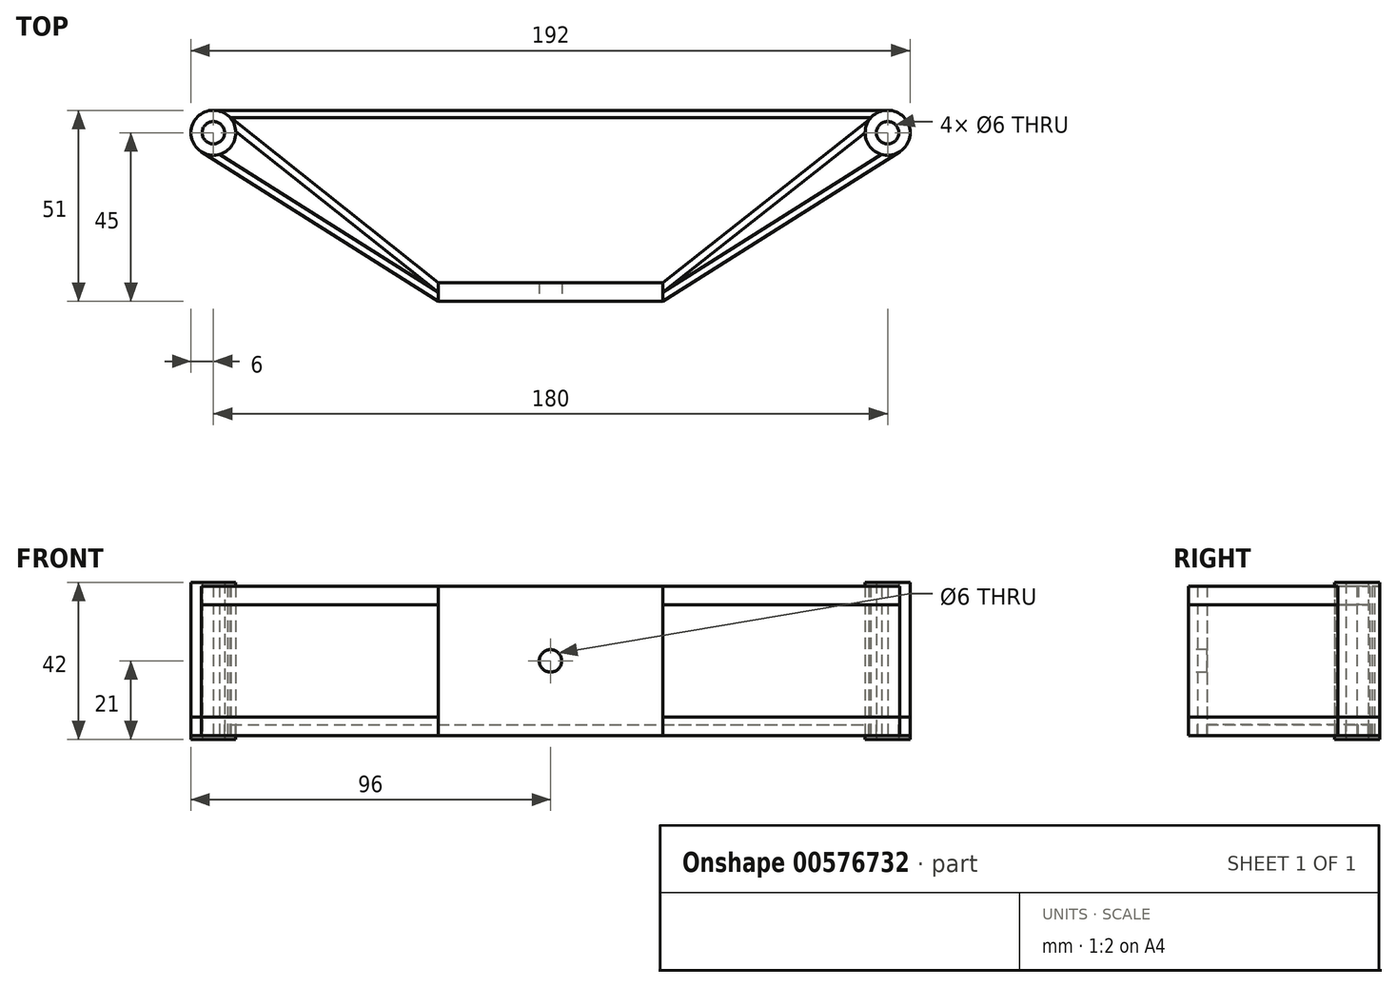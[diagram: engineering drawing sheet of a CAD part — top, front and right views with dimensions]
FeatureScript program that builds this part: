
annotation { "Feature Type Name" : "Feature", "Feature Type Description" : "" }
export const myFeature = defineFeature(function(context is Context, id is Id, definition is map)
    precondition{}
    {
        {
            var Q0;
            Q0=qCreatedBy(makeId("Top.planeOp"),FACE);
            var sketch = newSketch(context, id + "F0", { "sketchPlane" : qUnion([Q0])});
            skLineSegment(sketch, "E0.bottom", {"start": v(-30, 0) * mm, "end": v(30, 0) * mm});
            skLineSegment(sketch, "E0.top", {"start": v(-30, 5) * mm, "end": v(30, 5) * mm});
            skLineSegment(sketch, "E0.left", {"start": v(-30, 0) * mm, "end": v(-30, 5) * mm});
            skLineSegment(sketch, "E0.right", {"start": v(30, 0) * mm, "end": v(30, 5) * mm});
            skCircle(sketch, "E1", {"center": v(-90, 45) * mm, "radius": 3 * mm});
            skCircle(sketch, "E2", {"center": v(-90, 45) * mm, "radius": 6 * mm});
            skCircle(sketch, "E3", {"center": v(90, 45) * mm, "radius": 3 * mm});
            skCircle(sketch, "E4", {"center": v(90, 45) * mm, "radius": 6 * mm});
            skLineSegment(sketch, "E5", {"start": v(30, 0) * mm, "end": v(93.2, 39.93) * mm});
            skLineSegment(sketch, "E6", {"start": v(30, 5) * mm, "end": v(85.02, 48.35) * mm});
            skLineSegment(sketch, "E7", {"start": v(-30, 0) * mm, "end": v(-93.2, 39.93) * mm});
            skLineSegment(sketch, "E8", {"start": v(-90, 51) * mm, "end": v(90, 51) * mm});
            skLineSegment(sketch, "E9", {"start": v(-86.27, 49.7) * mm, "end": v(-30, 5) * mm});
            skLineSegment(sketch, "E10", {"start": v(-88.36, 39.23) * mm, "end": v(-30, 2.37) * mm});
            skLineSegment(sketch, "E11", {"start": v(-84.01, 45.35) * mm, "end": v(-30, 2.45) * mm});
            skLineSegment(sketch, "E12", {"start": v(84, 45) * mm, "end": v(30, 2.45) * mm});
            skLineSegment(sketch, "E13", {"start": v(88.36, 39.23) * mm, "end": v(30, 2.37) * mm});
            skLineSegment(sketch, "E14", {"start": v(-85.53, 49) * mm, "end": v(85.53, 49) * mm});
            skSolve(sketch);
        }
        {
            var Q0;
            Q0=makeQuery(id+"F0.imprint","IMPRINT",FACE,{"disambiguationData":[TD([[makeQuery(id+"F0.imprint","IMPRINT",EDGE,{"derivedFrom":sQuery(id+"F0.wireOp",EDGE,"E1")}),-1.0]])]});
            var Q1;
            Q1=makeQuery(id+"F0.imprint","IMPRINT",FACE,{"disambiguationData":[TD([[makeQuery(id+"F0.imprint","IMPRINT",EDGE,{"derivedFrom":sQuery(id+"F0.wireOp",EDGE,"E3")}),-1.0]])]});
            var Q2;
            Q2=makeQuery(id+"F0.imprint","IMPRINT",FACE,{"disambiguationData":[TD([[makeQuery(id+"F0.imprint","IMPRINT",EDGE,{"derivedFrom":sQuery(id+"F0.wireOp",EDGE,"E0.right")}),-1.0]])]});
            var Q3;
            Q3=makeQuery(id+"F0.imprint","IMPRINT",FACE,{"disambiguationData":[TD([[makeQuery(id+"F0.imprint","IMPRINT",EDGE,{"derivedFrom":sQuery(id+"F0.wireOp",EDGE,"E0.left")}),1.0]])]});
            extrude(context, id + "F1", {"entities" : qUnion([Q0, Q1, Q2, Q3]), "oppositeDirection" : true, "depth" : 20 * mm, "offsetDistance" : 25 * mm, "hasSecondDirection" : true, "secondDirectionOppositeDirection" : true, "secondDirectionDepth" : 15 * mm});
        }
        {
            var Q0;
            Q0=makeQuery(id+"F0.imprint","IMPRINT",FACE,{"disambiguationData":[TD([[makeQuery(id+"F0.imprint","IMPRINT",EDGE,{"derivedFrom":sQuery(id+"F0.wireOp",EDGE,"E0.bottom")}),1.0]])]});
            extrude(context, id + "F2", {"entities" : qUnion([Q0]), "endBound" : BoundingType.SYMMETRIC, "depth" : 40 * mm, "offsetDistance" : 25 * mm});
        }
        {
            var Q0;
            Q0=makeQuery(id+"F0.imprint","IMPRINT",FACE,{"disambiguationData":[TD([[makeQuery(id+"F0.imprint","IMPRINT",EDGE,{"derivedFrom":sQuery(id+"F0.wireOp",EDGE,"E0.top")}),1.0]])]});
            extrude(context, id + "F3", {"entities" : qUnion([Q0]), "oppositeDirection" : true, "depth" : 20 * mm, "offsetDistance" : 25 * mm, "hasSecondDirection" : true, "secondDirectionOppositeDirection" : true, "secondDirectionDepth" : 17 * mm});
        }
        {
            var Q0;
            Q0=makeQuery(id+"F0.imprint","IMPRINT",FACE,{"disambiguationData":[TD([[makeQuery(id+"F0.imprint","IMPRINT",EDGE,{"derivedFrom":sQuery(id+"F0.wireOp",EDGE,"E0.left")}),1.0]])]});
            var Q1;
            Q1=makeQuery(id+"F0.imprint","IMPRINT",FACE,{"disambiguationData":[TD([[makeQuery(id+"F0.imprint","IMPRINT",EDGE,{"derivedFrom":sQuery(id+"F0.wireOp",EDGE,"E0.right")}),-1.0]])]});
            extrude(context, id + "F4", {"entities" : qUnion([Q0, Q1]), "operationType" : NewBodyOperationType.ADD, "depth" : 20 * mm, "offsetDistance" : 25 * mm, "hasSecondDirection" : true, "secondDirectionOppositeDirection" : false, "secondDirectionDepth" : 15 * mm});
        }
        {
            var Q0;
            Q0=makeQuery(id+"F0.imprint","IMPRINT",FACE,{"disambiguationData":[TD([[makeQuery(id+"F0.imprint","IMPRINT",EDGE,{"derivedFrom":sQuery(id+"F0.wireOp",EDGE,"E1")}),-1.0]])]});
            var Q1;
            Q1=makeQuery(id+"F0.imprint","IMPRINT",FACE,{"disambiguationData":[TD([[makeQuery(id+"F0.imprint","IMPRINT",EDGE,{"derivedFrom":sQuery(id+"F0.wireOp",EDGE,"E3")}),-1.0]])]});
            extrude(context, id + "F5", {"entities" : qUnion([Q0, Q1]), "depth" : 21 * mm, "offsetDistance" : 25 * mm, "hasSecondDirection" : true, "secondDirectionOppositeDirection" : true, "secondDirectionDepth" : 21 * mm});
        }
        {
            var Q0;
            Q0=qCreatedBy(makeId("Front.planeOp"),FACE);
            var sketch = newSketch(context, id + "F6", { "sketchPlane" : qUnion([Q0])});
            skCircle(sketch, "E15", {"center": v(0, 0) * mm, "radius": 3 * mm});
            skSolve(sketch);
        }
        {
            var Q0;
            Q0=makeQuery(id+"F6.imprint","IMPRINT",FACE,{"disambiguationData":[TD([[makeQuery(id+"F6.imprint","IMPRINT",EDGE,{"derivedFrom":sQuery(id+"F6.wireOp",EDGE,"E15")}),1.0]])]});
            extrude(context, id + "F7", {"entities" : qUnion([Q0]), "operationType" : NewBodyOperationType.REMOVE, "oppositeDirection" : true, "depth" : 5 * mm, "offsetDistance" : 25 * mm});
        }
        {
            var Q0;
            {var subQ0=sQuery(id+"F0.wireOp",EDGE,"E7");Q0=makeQuery(id+"F0.imprint","IMPRINT",FACE,{"disambiguationData":[TD([[makeQuery(id+"F0.imprint","IMPRINT",EDGE,{"derivedFrom":subQ0}),-1.0]])]});}
            var Q1;
            {var subQ0=sQuery(id+"F0.wireOp",EDGE,"E9");Q1=makeQuery(id+"F0.imprint","IMPRINT",FACE,{"disambiguationData":[TD([[makeQuery(id+"F0.imprint","IMPRINT",EDGE,{"derivedFrom":subQ0}),-1.0]])]});}
            var Q2;
            {var subQ0=sQuery(id+"F0.wireOp",EDGE,"E5");Q2=makeQuery(id+"F0.imprint","IMPRINT",FACE,{"disambiguationData":[TD([[makeQuery(id+"F0.imprint","IMPRINT",EDGE,{"derivedFrom":subQ0}),1.0]])]});}
            var Q3;
            {var subQ0=sQuery(id+"F0.wireOp",EDGE,"E6");Q3=makeQuery(id+"F0.imprint","IMPRINT",FACE,{"disambiguationData":[TD([[makeQuery(id+"F0.imprint","IMPRINT",EDGE,{"derivedFrom":subQ0}),-1.0]])]});}
            extrude(context, id + "F8", {"entities" : qUnion([Q0, Q1, Q2, Q3]), "depth" : 20 * mm, "offsetDistance" : 25 * mm, "hasSecondDirection" : true, "secondDirectionOppositeDirection" : true, "secondDirectionDepth" : 20 * mm});
        }
        {
            var Q0;
            {var subQ0=sQuery(id+"F0.wireOp",EDGE,"E8");Q0=makeQuery(id+"F0.imprint","IMPRINT",FACE,{"disambiguationData":[TD([[makeQuery(id+"F0.imprint","IMPRINT",EDGE,{"derivedFrom":subQ0}),-1.0]])]});}
            extrude(context, id + "F9", {"entities" : qUnion([Q0]), "depth" : 20 * mm, "offsetDistance" : 25 * mm, "hasSecondDirection" : true, "secondDirectionOppositeDirection" : true, "secondDirectionDepth" : 20 * mm});
        }
    });
